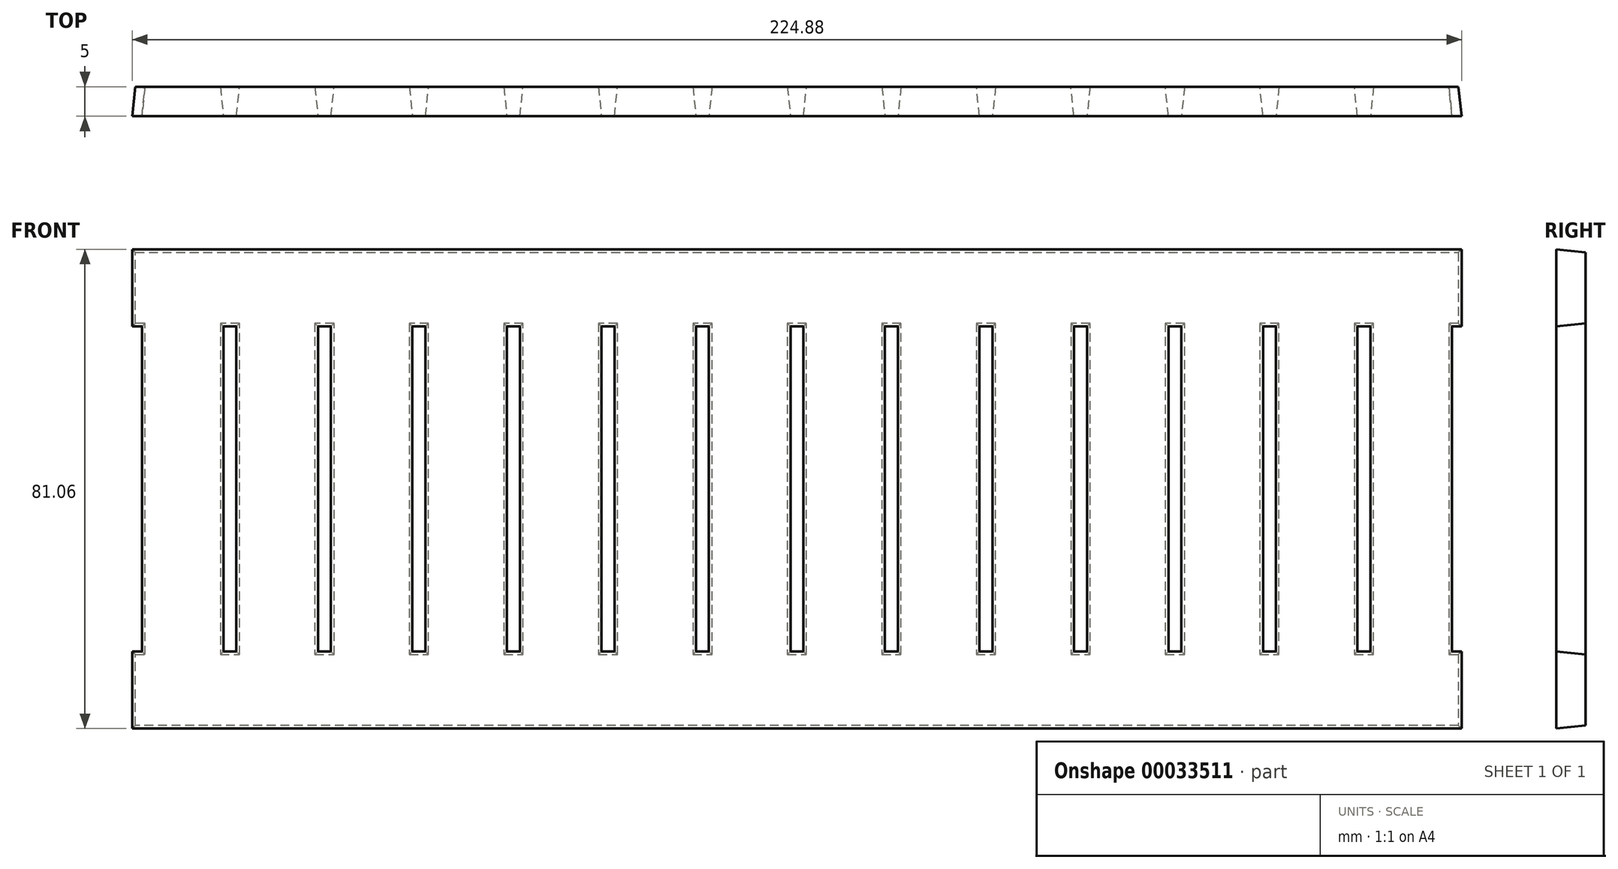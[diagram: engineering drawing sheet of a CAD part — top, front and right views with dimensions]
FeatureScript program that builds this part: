
annotation { "Feature Type Name" : "Feature", "Feature Type Description" : "" }
export const myFeature = defineFeature(function(context is Context, id is Id, definition is map)
    precondition{}
    {
        {
            var Q0;
            Q0=qCreatedBy(makeId("Front.planeOp"),FACE);
            var sketch = newSketch(context, id + "F0", { "sketchPlane" : qUnion([Q0])});
            skLineSegment(sketch, "E0.rect.bottom", {"start": v(111.92, 40) * mm, "end": v(-111.92, 40) * mm});
            skLineSegment(sketch, "E0.rect.top", {"start": v(111.92, -40) * mm, "end": v(-111.92, -40) * mm});
            skLineSegment(sketch, "E0.rect.left", {"start": v(111.92, 40) * mm, "end": v(111.92, -40) * mm});
            skLineSegment(sketch, "E0.rect.right", {"start": v(-111.92, 40) * mm, "end": v(-111.92, -40) * mm});
            skPoint(sketch, "E0.rect.middle", {"position": v(0, 0) * mm});
            skSolve(sketch);
        }
        {
            var Q0;
            Q0 = qSketchRegion(id + "F0", true);
            extrude(context, id + "F1", {"entities" : qUnion([Q0]), "depth" : 5 * mm, "hasDraft" : true, "draftAngle" : 6 * degree});
        }
        {
            var Q0;
            Q0=makeQuery(id+"F1.opExtrude","CAP_FACE",FACE,{"disambiguationData":[OSD([sQuery(id+"F0.wireOp",EDGE,"E0.rect.bottom"),sQuery(id+"F0.wireOp",EDGE,"E0.rect.top"),sQuery(id+"F0.wireOp",EDGE,"E0.rect.left"),sQuery(id+"F0.wireOp",EDGE,"E0.rect.right")])],"isStart":false});
            var sketch = newSketch(context, id + "F2", { "sketchPlane" : qUnion([Q0])});
            skLineSegment(sketch, "E1.rect.bottom", {"start": v(1.1, -27.5) * mm, "end": v(-1.1, -27.5) * mm});
            skLineSegment(sketch, "E1.rect.top", {"start": v(1.1, 27.5) * mm, "end": v(-1.1, 27.5) * mm});
            skLineSegment(sketch, "E1.rect.left", {"start": v(1.1, -27.5) * mm, "end": v(1.1, 27.5) * mm});
            skLineSegment(sketch, "E1.rect.right", {"start": v(-1.1, -27.5) * mm, "end": v(-1.1, 27.5) * mm});
            skPoint(sketch, "E1.rect.middle", {"position": v(0, 0) * mm});
            skLineSegment(sketch, "E2.rect.bottom", {"start": v(-30.88, -27.5) * mm, "end": v(-33.08, -27.5) * mm});
            skLineSegment(sketch, "E2.rect.top", {"start": v(-30.88, 27.5) * mm, "end": v(-33.08, 27.5) * mm});
            skLineSegment(sketch, "E2.rect.left", {"start": v(-30.88, -27.5) * mm, "end": v(-30.88, 27.5) * mm});
            skLineSegment(sketch, "E2.rect.right", {"start": v(-33.08, -27.5) * mm, "end": v(-33.08, 27.5) * mm});
            skPoint(sketch, "E2.rect.middle", {"position": v(-31.98, 0) * mm});
            skLineSegment(sketch, "E3.rect.bottom", {"start": v(-46.87, -27.5) * mm, "end": v(-49.07, -27.5) * mm});
            skLineSegment(sketch, "E3.rect.top", {"start": v(-46.87, 27.5) * mm, "end": v(-49.07, 27.5) * mm});
            skLineSegment(sketch, "E3.rect.left", {"start": v(-46.87, -27.5) * mm, "end": v(-46.87, 27.5) * mm});
            skLineSegment(sketch, "E3.rect.right", {"start": v(-49.07, -27.5) * mm, "end": v(-49.07, 27.5) * mm});
            skPoint(sketch, "E3.rect.middle", {"position": v(-47.97, 0) * mm});
            skLineSegment(sketch, "E4.rect.bottom", {"start": v(-62.85, -27.5) * mm, "end": v(-65.05, -27.5) * mm});
            skLineSegment(sketch, "E4.rect.top", {"start": v(-62.85, 27.5) * mm, "end": v(-65.05, 27.5) * mm});
            skLineSegment(sketch, "E4.rect.left", {"start": v(-62.85, -27.5) * mm, "end": v(-62.85, 27.5) * mm});
            skLineSegment(sketch, "E4.rect.right", {"start": v(-65.05, -27.5) * mm, "end": v(-65.05, 27.5) * mm});
            skPoint(sketch, "E4.rect.middle", {"position": v(-63.95, 0) * mm});
            skLineSegment(sketch, "E5.rect.bottom", {"start": v(-78.84, -27.5) * mm, "end": v(-81.04, -27.5) * mm});
            skLineSegment(sketch, "E5.rect.top", {"start": v(-78.84, 27.5) * mm, "end": v(-81.04, 27.5) * mm});
            skLineSegment(sketch, "E5.rect.left", {"start": v(-78.84, -27.5) * mm, "end": v(-78.84, 27.5) * mm});
            skLineSegment(sketch, "E5.rect.right", {"start": v(-81.04, -27.5) * mm, "end": v(-81.04, 27.5) * mm});
            skPoint(sketch, "E5.rect.middle", {"position": v(-79.94, 0) * mm});
            skLineSegment(sketch, "E6.rect.bottom", {"start": v(-94.83, -27.5) * mm, "end": v(-97.03, -27.5) * mm});
            skLineSegment(sketch, "E6.rect.top", {"start": v(-94.83, 27.5) * mm, "end": v(-97.03, 27.5) * mm});
            skLineSegment(sketch, "E6.rect.left", {"start": v(-94.83, -27.5) * mm, "end": v(-94.83, 27.5) * mm});
            skLineSegment(sketch, "E6.rect.right", {"start": v(-97.03, -27.5) * mm, "end": v(-97.03, 27.5) * mm});
            skPoint(sketch, "E6.rect.middle", {"position": v(-95.93, 0) * mm});
            skLineSegment(sketch, "E7.rect.bottom", {"start": v(-17.09, -27.5) * mm, "end": v(-14.89, -27.5) * mm});
            skLineSegment(sketch, "E7.rect.top", {"start": v(-17.09, 27.5) * mm, "end": v(-14.89, 27.5) * mm});
            skLineSegment(sketch, "E7.rect.left", {"start": v(-17.09, -27.5) * mm, "end": v(-17.09, 27.5) * mm});
            skLineSegment(sketch, "E7.rect.right", {"start": v(-14.89, -27.5) * mm, "end": v(-14.89, 27.5) * mm});
            skPoint(sketch, "E7.rect.middle", {"position": v(-15.99, 0) * mm});
            skLineSegment(sketch, "E8.rect.bottom", {"start": v(-110.82, -27.5) * mm, "end": v(-113.02, -27.5) * mm});
            skLineSegment(sketch, "E8.rect.top", {"start": v(-110.82, 27.5) * mm, "end": v(-113.02, 27.5) * mm});
            skLineSegment(sketch, "E8.rect.left", {"start": v(-110.82, -27.5) * mm, "end": v(-110.82, 27.5) * mm});
            skLineSegment(sketch, "E8.rect.right", {"start": v(-113.02, -27.5) * mm, "end": v(-113.02, 27.5) * mm});
            skPoint(sketch, "E8.rect.middle", {"position": v(-111.92, 0) * mm});
            skLineSegment(sketch, "E9.rect.bottom", {"start": v(17.09, 27.5) * mm, "end": v(14.89, 27.5) * mm});
            skLineSegment(sketch, "E9.rect.top", {"start": v(17.09, -27.5) * mm, "end": v(14.89, -27.5) * mm});
            skLineSegment(sketch, "E9.rect.left", {"start": v(17.09, 27.5) * mm, "end": v(17.09, -27.5) * mm});
            skLineSegment(sketch, "E9.rect.right", {"start": v(14.89, 27.5) * mm, "end": v(14.89, -27.5) * mm});
            skPoint(sketch, "E9.rect.middle", {"position": v(15.99, 0) * mm});
            skLineSegment(sketch, "E10.rect.bottom", {"start": v(30.88, 27.5) * mm, "end": v(33.08, 27.5) * mm});
            skLineSegment(sketch, "E10.rect.top", {"start": v(30.88, -27.5) * mm, "end": v(33.08, -27.5) * mm});
            skLineSegment(sketch, "E10.rect.left", {"start": v(30.88, 27.5) * mm, "end": v(30.88, -27.5) * mm});
            skLineSegment(sketch, "E10.rect.right", {"start": v(33.08, 27.5) * mm, "end": v(33.08, -27.5) * mm});
            skPoint(sketch, "E10.rect.middle", {"position": v(31.98, 0) * mm});
            skLineSegment(sketch, "E11.rect.bottom", {"start": v(46.87, 27.5) * mm, "end": v(49.07, 27.5) * mm});
            skLineSegment(sketch, "E11.rect.top", {"start": v(46.87, -27.5) * mm, "end": v(49.07, -27.5) * mm});
            skLineSegment(sketch, "E11.rect.left", {"start": v(46.87, 27.5) * mm, "end": v(46.87, -27.5) * mm});
            skLineSegment(sketch, "E11.rect.right", {"start": v(49.07, 27.5) * mm, "end": v(49.07, -27.5) * mm});
            skPoint(sketch, "E11.rect.middle", {"position": v(47.97, 0) * mm});
            skLineSegment(sketch, "E12.rect.bottom", {"start": v(62.85, 27.5) * mm, "end": v(65.05, 27.5) * mm});
            skLineSegment(sketch, "E12.rect.top", {"start": v(62.85, -27.5) * mm, "end": v(65.05, -27.5) * mm});
            skLineSegment(sketch, "E12.rect.left", {"start": v(62.85, 27.5) * mm, "end": v(62.85, -27.5) * mm});
            skLineSegment(sketch, "E12.rect.right", {"start": v(65.05, 27.5) * mm, "end": v(65.05, -27.5) * mm});
            skPoint(sketch, "E12.rect.middle", {"position": v(63.95, 0) * mm});
            skLineSegment(sketch, "E13.rect.bottom", {"start": v(78.84, 27.5) * mm, "end": v(81.04, 27.5) * mm});
            skLineSegment(sketch, "E13.rect.top", {"start": v(78.84, -27.5) * mm, "end": v(81.04, -27.5) * mm});
            skLineSegment(sketch, "E13.rect.left", {"start": v(78.84, 27.5) * mm, "end": v(78.84, -27.5) * mm});
            skLineSegment(sketch, "E13.rect.right", {"start": v(81.04, 27.5) * mm, "end": v(81.04, -27.5) * mm});
            skPoint(sketch, "E13.rect.middle", {"position": v(79.94, 0) * mm});
            skLineSegment(sketch, "E14.rect.bottom", {"start": v(94.83, 27.5) * mm, "end": v(97.03, 27.5) * mm});
            skLineSegment(sketch, "E14.rect.top", {"start": v(94.83, -27.5) * mm, "end": v(97.03, -27.5) * mm});
            skLineSegment(sketch, "E14.rect.left", {"start": v(94.83, 27.5) * mm, "end": v(94.83, -27.5) * mm});
            skLineSegment(sketch, "E14.rect.right", {"start": v(97.03, 27.5) * mm, "end": v(97.03, -27.5) * mm});
            skPoint(sketch, "E14.rect.middle", {"position": v(95.93, 0) * mm});
            skLineSegment(sketch, "E15.rect.bottom", {"start": v(110.82, 27.5) * mm, "end": v(113.02, 27.5) * mm});
            skLineSegment(sketch, "E15.rect.top", {"start": v(110.82, -27.5) * mm, "end": v(113.02, -27.5) * mm});
            skLineSegment(sketch, "E15.rect.left", {"start": v(110.82, 27.5) * mm, "end": v(110.82, -27.5) * mm});
            skLineSegment(sketch, "E15.rect.right", {"start": v(113.02, 27.5) * mm, "end": v(113.02, -27.5) * mm});
            skPoint(sketch, "E15.rect.middle", {"position": v(111.92, 0) * mm});
            skLineSegment(sketch, "E16", {"start": v(-110.82, 27.5) * mm, "end": v(-97.03, 27.5) * mm, "construction": true});
            skLineSegment(sketch, "E17", {"start": v(-94.83, 27.5) * mm, "end": v(-81.04, 27.5) * mm, "construction": true});
            skLineSegment(sketch, "E18", {"start": v(-78.84, 27.5) * mm, "end": v(-65.05, 27.5) * mm, "construction": true});
            skLineSegment(sketch, "E19", {"start": v(-62.85, 27.5) * mm, "end": v(-49.07, 27.5) * mm, "construction": true});
            skLineSegment(sketch, "E20", {"start": v(-46.87, 27.5) * mm, "end": v(-33.08, 27.5) * mm, "construction": true});
            skLineSegment(sketch, "E21", {"start": v(-30.88, 27.5) * mm, "end": v(-17.09, 27.5) * mm, "construction": true});
            skLineSegment(sketch, "E22", {"start": v(-14.89, 27.5) * mm, "end": v(-1.1, 27.5) * mm, "construction": true});
            skLineSegment(sketch, "E23", {"start": v(1.1, 27.5) * mm, "end": v(14.89, 27.5) * mm, "construction": true});
            skLineSegment(sketch, "E24", {"start": v(17.09, 27.5) * mm, "end": v(30.88, 27.5) * mm, "construction": true});
            skLineSegment(sketch, "E25", {"start": v(33.08, 27.5) * mm, "end": v(46.87, 27.5) * mm, "construction": true});
            skLineSegment(sketch, "E26", {"start": v(49.07, 27.5) * mm, "end": v(62.85, 27.5) * mm, "construction": true});
            skLineSegment(sketch, "E27", {"start": v(65.05, 27.5) * mm, "end": v(78.84, 27.5) * mm, "construction": true});
            skLineSegment(sketch, "E28", {"start": v(81.04, 27.5) * mm, "end": v(94.83, 27.5) * mm, "construction": true});
            skLineSegment(sketch, "E29", {"start": v(97.03, 27.5) * mm, "end": v(110.82, 27.5) * mm, "construction": true});
            skSolve(sketch);
        }
        {
            var Q0;
            Q0=makeQuery(id+"F2.imprint","IMPRINT",FACE,{"disambiguationData":[TD([[makeQuery(id+"F2.imprint","IMPRINT",EDGE,{"derivedFrom":sQuery(id+"F2.wireOp",EDGE,"E6.rect.bottom")}),-1.0]])]});
            var Q1;
            {var subQ5=sQuery(id+"F2.wireOp",EDGE,"E8.rect.left");Q1=makeQuery(id+"F2.imprint","IMPRINT",FACE,{"disambiguationData":[TD([[makeQuery(id+"F2.imprint","IMPRINT",EDGE,{"derivedFrom":subQ5}),1.0]])]});}
            var Q2;
            Q2=makeQuery(id+"F2.imprint","IMPRINT",FACE,{"disambiguationData":[TD([[makeQuery(id+"F2.imprint","IMPRINT",EDGE,{"derivedFrom":sQuery(id+"F2.wireOp",EDGE,"E5.rect.bottom")}),-1.0]])]});
            var Q3;
            Q3=makeQuery(id+"F2.imprint","IMPRINT",FACE,{"disambiguationData":[TD([[makeQuery(id+"F2.imprint","IMPRINT",EDGE,{"derivedFrom":sQuery(id+"F2.wireOp",EDGE,"E4.rect.bottom")}),-1.0]])]});
            var Q4;
            Q4=makeQuery(id+"F2.imprint","IMPRINT",FACE,{"disambiguationData":[TD([[makeQuery(id+"F2.imprint","IMPRINT",EDGE,{"derivedFrom":sQuery(id+"F2.wireOp",EDGE,"E3.rect.bottom")}),-1.0]])]});
            var Q5;
            Q5=makeQuery(id+"F2.imprint","IMPRINT",FACE,{"disambiguationData":[TD([[makeQuery(id+"F2.imprint","IMPRINT",EDGE,{"derivedFrom":sQuery(id+"F2.wireOp",EDGE,"E2.rect.bottom")}),-1.0]])]});
            var Q6;
            Q6=makeQuery(id+"F2.imprint","IMPRINT",FACE,{"disambiguationData":[TD([[makeQuery(id+"F2.imprint","IMPRINT",EDGE,{"derivedFrom":sQuery(id+"F2.wireOp",EDGE,"E7.rect.bottom")}),1.0]])]});
            var Q7;
            Q7=makeQuery(id+"F2.imprint","IMPRINT",FACE,{"disambiguationData":[TD([[makeQuery(id+"F2.imprint","IMPRINT",EDGE,{"derivedFrom":sQuery(id+"F2.wireOp",EDGE,"E1.rect.bottom")}),-1.0]])]});
            var Q8;
            Q8=makeQuery(id+"F2.imprint","IMPRINT",FACE,{"disambiguationData":[TD([[makeQuery(id+"F2.imprint","IMPRINT",EDGE,{"derivedFrom":sQuery(id+"F2.wireOp",EDGE,"E9.rect.bottom")}),1.0]])]});
            var Q9;
            Q9=makeQuery(id+"F2.imprint","IMPRINT",FACE,{"disambiguationData":[TD([[makeQuery(id+"F2.imprint","IMPRINT",EDGE,{"derivedFrom":sQuery(id+"F2.wireOp",EDGE,"E10.rect.bottom")}),-1.0]])]});
            var Q10;
            Q10=makeQuery(id+"F2.imprint","IMPRINT",FACE,{"disambiguationData":[TD([[makeQuery(id+"F2.imprint","IMPRINT",EDGE,{"derivedFrom":sQuery(id+"F2.wireOp",EDGE,"E12.rect.bottom")}),-1.0]])]});
            var Q11;
            Q11=makeQuery(id+"F2.imprint","IMPRINT",FACE,{"disambiguationData":[TD([[makeQuery(id+"F2.imprint","IMPRINT",EDGE,{"derivedFrom":sQuery(id+"F2.wireOp",EDGE,"E11.rect.bottom")}),-1.0]])]});
            var Q12;
            Q12=makeQuery(id+"F2.imprint","IMPRINT",FACE,{"disambiguationData":[TD([[makeQuery(id+"F2.imprint","IMPRINT",EDGE,{"derivedFrom":sQuery(id+"F2.wireOp",EDGE,"E13.rect.bottom")}),-1.0]])]});
            var Q13;
            Q13=makeQuery(id+"F2.imprint","IMPRINT",FACE,{"disambiguationData":[TD([[makeQuery(id+"F2.imprint","IMPRINT",EDGE,{"derivedFrom":sQuery(id+"F2.wireOp",EDGE,"E14.rect.bottom")}),-1.0]])]});
            var Q14;
            {var subQ5=sQuery(id+"F2.wireOp",EDGE,"E15.rect.left");Q14=makeQuery(id+"F2.imprint","IMPRINT",FACE,{"disambiguationData":[TD([[makeQuery(id+"F2.imprint","IMPRINT",EDGE,{"derivedFrom":subQ5}),1.0]])]});}
            extrude(context, id + "F3", {"entities" : qUnion([Q0, Q1, Q2, Q3, Q4, Q5, Q6, Q7, Q8, Q9, Q10, Q11, Q12, Q13, Q14]), "operationType" : NewBodyOperationType.REMOVE, "oppositeDirection" : true, "depth" : 25 * mm, "hasDraft" : true, "draftAngle" : 6 * degree});
        }
    });
